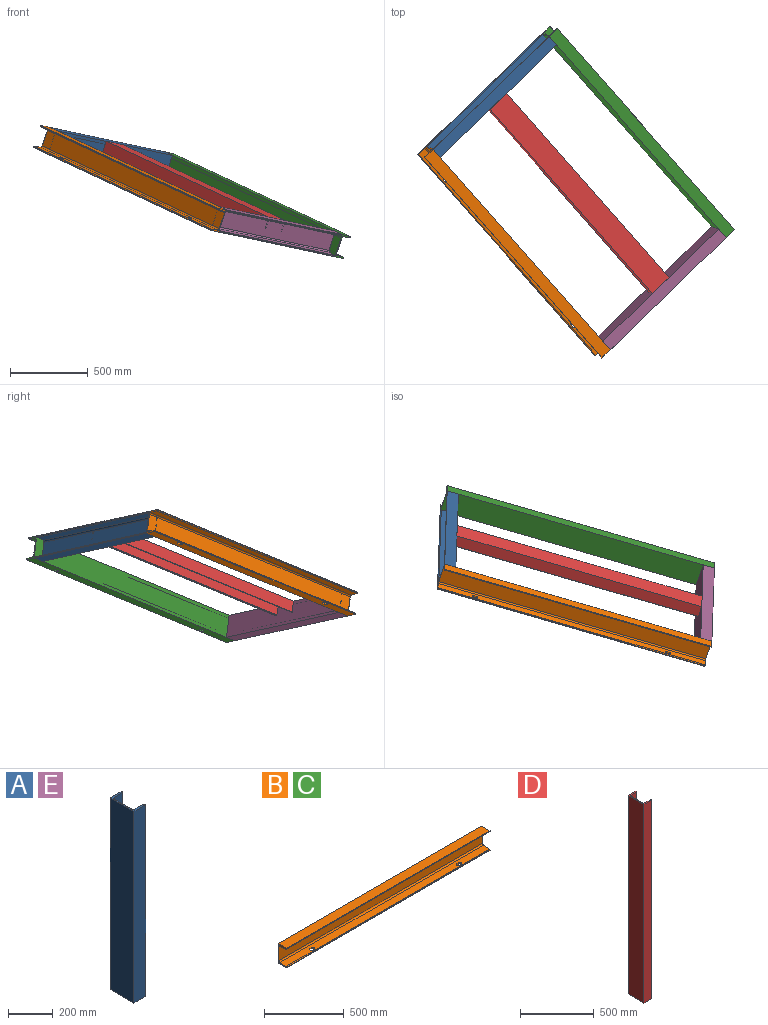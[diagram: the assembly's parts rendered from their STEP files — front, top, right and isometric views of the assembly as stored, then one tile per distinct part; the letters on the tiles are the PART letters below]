
ASSEMBLY  parts=5 mates=4
PART A: 14 faces, bbox 75x150x1050 mm
  f0: plane 1050x107.77mm, normal (1,0,0), area 113160mm2, adj f1,f11,f12,f13
  f1: cylinder r=10mm len=1050mm, axis (0,0,1), area 15943.6mm2, adj f0,f2,f12,f13
  f2: plane 1050x54.29mm, normal (0.05,-1,0), area 57077.5mm2, adj f1,f3,f12,f13
  f3: cylinder r=5mm len=1050mm, axis (0,0,1), area 7971.8mm2, adj f2,f4,f12,f13
  f4: plane 1050x3.29mm, normal (1,0,0), area 3454.4mm2, adj f3,f5,f12,f13
  f5: plane 1050x75mm, normal (0,1,0), area 78750mm2, adj f4,f6,f12,f13
  f6: plane 1050x150mm, normal (-1,0,0), area 157500mm2, adj f5,f7,f12,f13
  f7: plane 1050x75mm, normal (0,-1,0), area 78750mm2, adj f6,f8,f12,f13
  f8: plane 1050x3.29mm, normal (1,0,0), area 3454.4mm2, adj f7,f9,f12,f13
  f9: cylinder r=5mm len=1050mm, axis (0,0,1), area 7971.8mm2, adj f8,f10,f12,f13
  f10: plane 1050x54.29mm, normal (0.05,1,0), area 57077.5mm2, adj f9,f11,f12,f13
  f11: cylinder r=10mm len=1050mm, axis (0,0,1), area 15943.6mm2, adj f0,f10,f12,f13
  f12: plane 150x75mm, normal (0,0,-1), area 2350.1mm2, adj f0,f1,f2,f3,f4,f5,f6,f7
  f13: plane 150x75mm, normal (0,0,1), area 2350.1mm2, adj f0,f1,f2,f3,f4,f5,f6,f7
PART B: 22 faces, bbox 1800x75x150 mm
  f0: plane 1800x54.29mm, normal (0,-0.05,1), area 96513.1mm2, adj f2,f11,f12,f13,f14,f15,f16,f17
  f1: plane 1800x75mm, normal (0,0,-1), area 133667.7mm2, adj f3,f4,f12,f13,f14,f15,f16,f17
  f2: cylinder r=5mm len=1800mm, axis (-1,0,0), area 13665.9mm2, adj f0,f3,f12,f13
  f3: plane 1800x3.29mm, normal (0,-1,0), area 5921.8mm2, adj f1,f2,f12,f13
  f4: plane 1800x150mm, normal (0,1,0), area 270000mm2, adj f1,f5,f12,f13
  f5: plane 1800x75mm, normal (0,0,1), area 135000mm2, adj f4,f6,f12,f13
  f6: plane 1800x3.29mm, normal (0,-1,0), area 5921.8mm2, adj f5,f7,f12,f13
  f7: cylinder r=5mm len=1800mm, axis (-1,0,0), area 13665.9mm2, adj f6,f8,f12,f13
  f8: plane 1800x54.29mm, normal (0,-0.05,-1), area 97847.2mm2, adj f7,f9,f12,f13
  f9: cylinder r=10mm len=1800mm, axis (-1,0,0), area 27331.9mm2, adj f8,f10,f12,f13
  f10: plane 1800x107.77mm, normal (0,-1,0), area 193988.6mm2, adj f9,f11,f12,f13
  f11: cylinder r=10mm len=1800mm, axis (-1,0,0), area 27331.9mm2, adj f0,f10,f12,f13
  f12: plane 150x75mm, normal (1,0,0), area 2350.1mm2, adj f0,f1,f2,f3,f4,f5,f6,f7
  f13: plane 150x75mm, normal (-1,0,0), area 2350.1mm2, adj f0,f1,f2,f3,f4,f5,f6,f7
  f14: cylinder r=11mm len=22mm, axis (0,0,-1), area 322.9mm2, adj f0,f1,f15,f17
  f15: plane 13x8.77mm, normal (0,1,0), area 114mm2, adj f0,f1,f14,f16
  f16: cylinder r=11mm len=22mm, axis (0,0,-1), area 322.9mm2, adj f0,f1,f15,f17
  f17: plane 13x9.92mm, normal (0,-1,0), area 129mm2, adj f0,f1,f14,f16
  f18: cylinder r=11mm len=22mm, axis (0,0,-1), area 322.9mm2, adj f0,f1,f19,f21
  f19: plane 13x9.92mm, normal (0,-1,0), area 129mm2, adj f0,f1,f18,f20
  f20: cylinder r=11mm len=22mm, axis (0,0,-1), area 322.9mm2, adj f0,f1,f19,f21
  f21: plane 13x8.77mm, normal (0,1,0), area 114mm2, adj f0,f1,f18,f20
PART C: same geometry as B
PART D: 14 faces, bbox 75x150x1650 mm
  f0: plane 1650x107.77mm, normal (1,0,0), area 177822.9mm2, adj f1,f11,f12,f13
  f1: cylinder r=10mm len=1650mm, axis (0,0,1), area 25054.2mm2, adj f0,f2,f12,f13
  f2: plane 1650x54.29mm, normal (0.05,-1,0), area 89693.2mm2, adj f1,f3,f12,f13
  f3: cylinder r=5mm len=1650mm, axis (0,0,1), area 12527.1mm2, adj f2,f4,f12,f13
  f4: plane 1650x3.29mm, normal (1,0,0), area 5428.3mm2, adj f3,f5,f12,f13
  f5: plane 1650x75mm, normal (0,1,0), area 123750mm2, adj f4,f6,f12,f13
  f6: plane 1650x150mm, normal (-1,0,0), area 247500mm2, adj f5,f7,f12,f13
  f7: plane 1650x75mm, normal (0,-1,0), area 123750mm2, adj f6,f8,f12,f13
  f8: plane 1650x3.29mm, normal (1,0,0), area 5428.3mm2, adj f7,f9,f12,f13
  f9: cylinder r=5mm len=1650mm, axis (0,0,1), area 12527.1mm2, adj f8,f10,f12,f13
  f10: plane 1650x54.29mm, normal (0.05,1,0), area 89693.2mm2, adj f9,f11,f12,f13
  f11: cylinder r=10mm len=1650mm, axis (0,0,1), area 25054.2mm2, adj f0,f10,f12,f13
  f12: plane 150x75mm, normal (0,0,-1), area 2350.1mm2, adj f0,f1,f2,f3,f4,f5,f6,f7
  f13: plane 150x75mm, normal (0,0,1), area 2350.1mm2, adj f0,f1,f2,f3,f4,f5,f6,f7
PART E: same geometry as A
PLACE A rot(axis=(0.4,0.65,0.64),161.5deg) t=(-255.95,945.71,186.51)mm
PLACE B rot(axis=(-0.02,0.39,-0.92),50.8deg) t=(-1063.22,16.84,340.99)mm
PLACE C rot(axis=(0.18,0.01,0.98),133.5deg) t=(1082.54,-295.35,-405.39)mm
PLACE D rot(axis=(0.32,0.89,-0.34),117.3deg) t=(526.6,-657.79,-461.54)mm
PLACE E rot(axis=(-0.83,0.51,-0.21),101.7deg) t=(973.66,-484.62,-551.29)mm
MATE planar C.f5 <-> A.f5  axis (0.31,-0.11,0.94) through (-186.5,866.95,154.07)mm
MATE planar A.f5 <-> D.f6  axis (0.31,-0.11,0.94) through (-511.67,451.95,211.36)mm
MATE planar B.f5 <-> A.f5  axis (0.31,-0.11,0.94) through (-931.63,144.43,312.93)mm
MATE planar C.f5 <-> E.f7  axis (0.31,-0.11,0.94) through (950.95,-422.94,-377.33)mm
